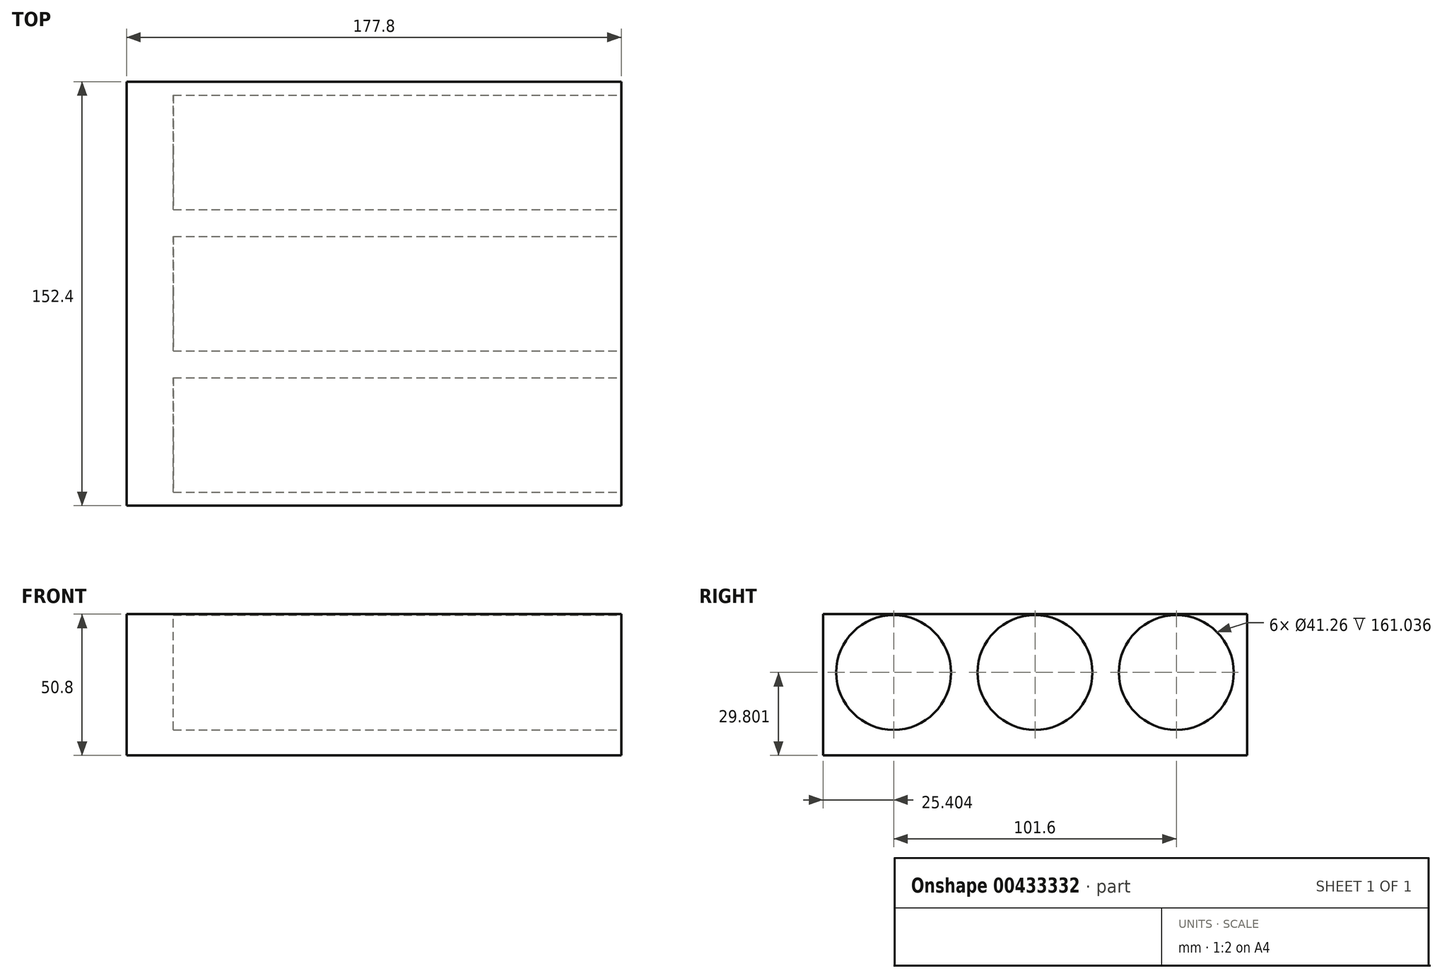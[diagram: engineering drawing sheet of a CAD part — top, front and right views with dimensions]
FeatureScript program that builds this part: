
annotation { "Feature Type Name" : "Feature", "Feature Type Description" : "" }
export const myFeature = defineFeature(function(context is Context, id is Id, definition is map)
    precondition{}
    {
        {
            var Q0;
            Q0=qCreatedBy(makeId("Top.planeOp"),FACE);
            var sketch = newSketch(context, id + "F0", { "sketchPlane" : qUnion([Q0])});
            skLineSegment(sketch, "E0.bottom", {"start": v(-75.73, 118.81) * mm, "end": v(102.07, 118.81) * mm});
            skLineSegment(sketch, "E0.top", {"start": v(-75.73, -33.59) * mm, "end": v(102.07, -33.59) * mm});
            skLineSegment(sketch, "E0.left", {"start": v(-75.73, 118.81) * mm, "end": v(-75.73, -33.59) * mm});
            skLineSegment(sketch, "E0.right", {"start": v(102.07, 118.81) * mm, "end": v(102.07, -33.59) * mm});
            skSolve(sketch);
        }
        {
            var Q0;
            Q0=makeQuery(id+"F0.imprint","IMPRINT",FACE,{"disambiguationData":[TD([[makeQuery(id+"F0.imprint","IMPRINT",EDGE,{"derivedFrom":sQuery(id+"F0.wireOp",EDGE,"E0.bottom")}),-1.0]])]});
            extrude(context, id + "F1", {"entities" : qUnion([Q0]), "depth" : 50.8 * mm});
        }
        {
            var Q0;
            Q0=makeQuery(id+"F1.opExtrude","SWEPT_FACE",FACE,{"disambiguationData":[OSD([sQuery(id+"F0.wireOp",EDGE,"E0.right")])]});
            var sketch = newSketch(context, id + "F2", { "sketchPlane" : qUnion([Q0])});
            skCircle(sketch, "E1", {"center": v(-8.19, 29.8) * mm, "radius": 20.63 * mm});
            skCircle(sketch, "E2.1.0.0", {"center": v(42.61, 29.8) * mm, "radius": 20.63 * mm});
            skCircle(sketch, "E2.2.0.0", {"center": v(93.41, 29.8) * mm, "radius": 20.63 * mm});
            skLineSegment(sketch, "E2.direction1", {"start": v(-8.19, 29.8) * mm, "end": v(42.61, 29.8) * mm, "construction": true});
            skSolve(sketch);
        }
        {
            var Q0;
            Q0 = qSketchRegion(id + "F2", true);
            extrude(context, id + "F3", {"entities" : qUnion([Q0]), "operationType" : NewBodyOperationType.REMOVE, "oppositeDirection" : true, "depth" : 161.04 * mm});
        }
    });
